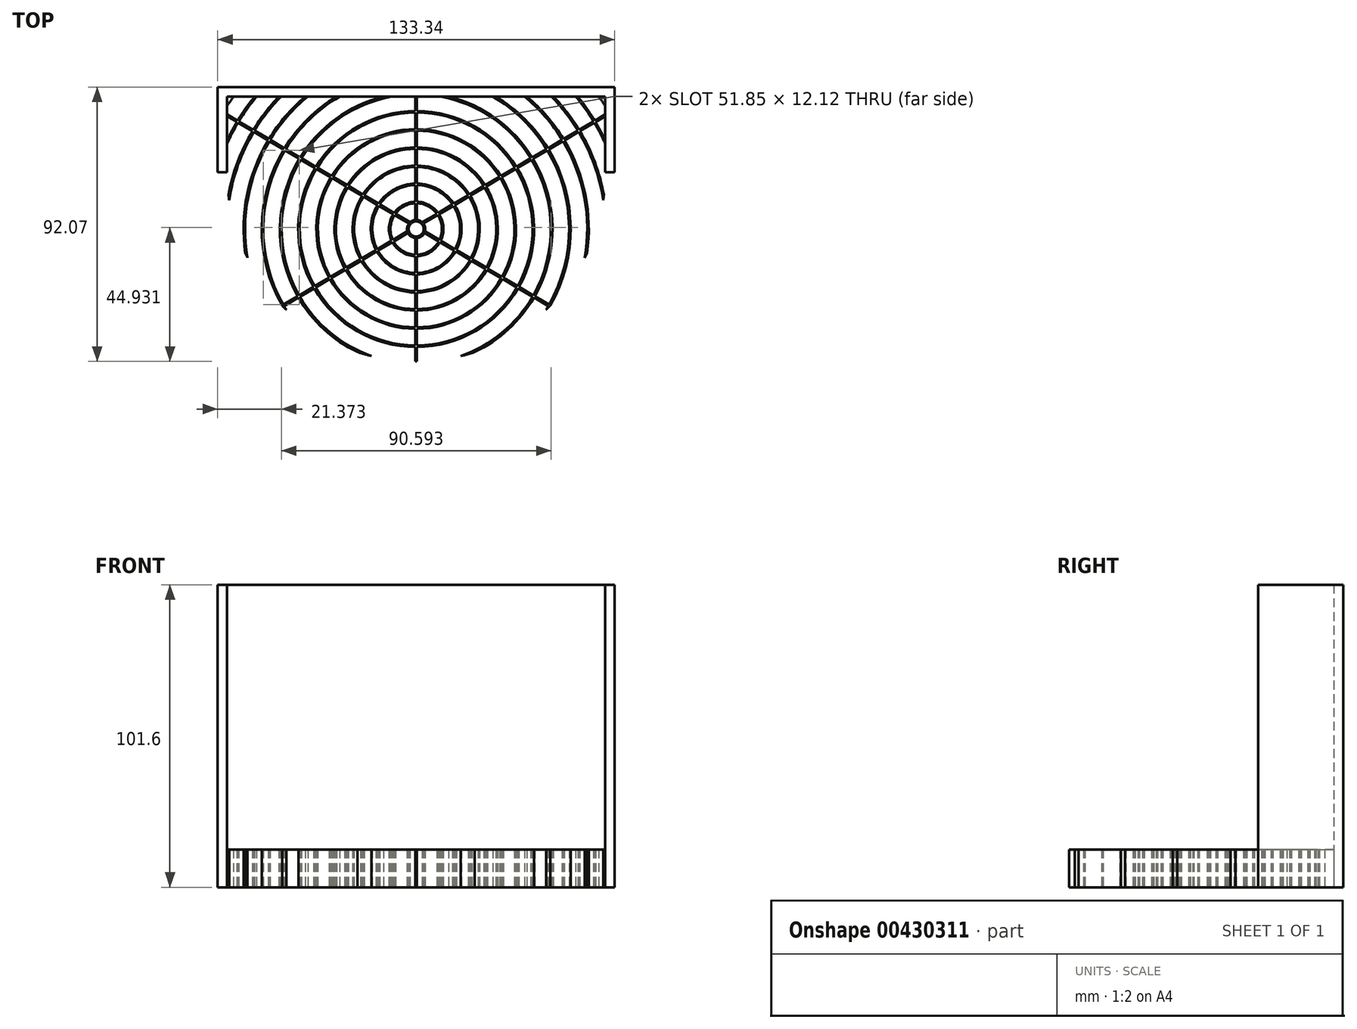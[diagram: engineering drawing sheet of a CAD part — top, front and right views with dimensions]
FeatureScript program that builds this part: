
annotation { "Feature Type Name" : "Feature", "Feature Type Description" : "" }
export const myFeature = defineFeature(function(context is Context, id is Id, definition is map)
    precondition{}
    {
        {
            var Q0;
            Q0=qCreatedBy(makeId("Top.planeOp"),FACE);
            var sketch = newSketch(context, id + "F0", { "sketchPlane" : qUnion([Q0])});
            skArc(sketch, "E0", {"start": v(63.5, 0) * mm, "mid": v(0, -63.5) * mm, "end": v(-63.5, 0) * mm});
            skArc(sketch, "E1.0", {"start": v(66.67, 0) * mm, "mid": v(0, -66.67) * mm, "end": v(-66.67, 0) * mm});
            skLineSegment(sketch, "E2.bottom", {"start": v(-66.67, 0) * mm, "end": v(-63.5, 0) * mm});
            skLineSegment(sketch, "E2.top", {"start": v(-66.67, 25.4) * mm, "end": v(-63.5, 25.4) * mm});
            skLineSegment(sketch, "E2.left", {"start": v(-66.67, 0) * mm, "end": v(-66.67, 25.4) * mm});
            skLineSegment(sketch, "E2.right", {"start": v(-63.5, 0) * mm, "end": v(-63.5, 25.4) * mm});
            skLineSegment(sketch, "E3.bottom", {"start": v(63.5, 0) * mm, "end": v(66.67, 0) * mm});
            skLineSegment(sketch, "E3.top", {"start": v(63.5, 25.4) * mm, "end": v(66.67, 25.4) * mm});
            skLineSegment(sketch, "E3.left", {"start": v(63.5, 0) * mm, "end": v(63.5, 25.4) * mm});
            skLineSegment(sketch, "E3.right", {"start": v(66.67, 0) * mm, "end": v(66.67, 25.4) * mm});
            skCircle(sketch, "E4", {"center": v(0, -19.05) * mm, "radius": 2.54 * mm});
            skArc(sketch, "E5.0", {"start": v(-0.25, -16.01) * mm, "mid": v(-1.22, -16.26) * mm, "end": v(-2.06, -16.8) * mm});
            skArc(sketch, "E6.0", {"start": v(-0.25, -10.42) * mm, "mid": v(-4, -11.4) * mm, "end": v(-6.95, -13.92) * mm});
            skArc(sketch, "E7.0", {"start": v(-0.25, -9.9) * mm, "mid": v(-4.26, -10.96) * mm, "end": v(-7.39, -13.66) * mm});
            skArc(sketch, "E8.0", {"start": v(-0.25, -4.32) * mm, "mid": v(-7.03, -6.1) * mm, "end": v(-12.22, -10.82) * mm});
            skArc(sketch, "E9.0", {"start": v(-0.25, -3.81) * mm, "mid": v(-7.28, -5.66) * mm, "end": v(-12.66, -10.56) * mm});
            skArc(sketch, "E10.0", {"start": v(-0.25, 1.78) * mm, "mid": v(-10.06, -0.81) * mm, "end": v(-17.48, -7.72) * mm});
            skArc(sketch, "E11.0", {"start": v(-0.25, 2.28) * mm, "mid": v(-10.3, -0.37) * mm, "end": v(-17.91, -7.46) * mm});
            skArc(sketch, "E12.0", {"start": v(-0.25, 7.87) * mm, "mid": v(-13.08, 4.48) * mm, "end": v(-22.73, -4.62) * mm});
            skArc(sketch, "E13.0", {"start": v(-0.25, 8.38) * mm, "mid": v(-13.33, 4.92) * mm, "end": v(-23.17, -4.36) * mm});
            skArc(sketch, "E14.0", {"start": v(-0.25, 13.97) * mm, "mid": v(-16.1, 9.78) * mm, "end": v(-27.99, -1.52) * mm});
            skArc(sketch, "E15.0", {"start": v(-0.25, 14.48) * mm, "mid": v(-16.36, 10.22) * mm, "end": v(-28.42, -1.27) * mm});
            skArc(sketch, "E16.0", {"start": v(-0.25, 20.07) * mm, "mid": v(-19.13, 15.07) * mm, "end": v(-33.24, 1.57) * mm});
            skArc(sketch, "E17.0", {"start": v(-0.25, 20.57) * mm, "mid": v(-19.38, 15.51) * mm, "end": v(-33.68, 1.83) * mm});
            skLineSegment(sketch, "E18.bottom", {"start": v(-66.67, 25.4) * mm, "end": v(66.67, 25.4) * mm});
            skLineSegment(sketch, "E18.top", {"start": v(-66.67, 28.57) * mm, "end": v(66.67, 28.57) * mm});
            skLineSegment(sketch, "E18.left", {"start": v(-66.67, 25.4) * mm, "end": v(-66.67, 28.57) * mm});
            skLineSegment(sketch, "E18.right", {"start": v(66.67, 25.4) * mm, "end": v(66.67, 28.57) * mm});
            skArc(sketch, "E19.0", {"start": v(14.98, -61.7) * mm, "mid": v(28.8, -53.9) * mm, "end": v(39.07, -41.8) * mm});
            skArc(sketch, "E20.0", {"start": v(19.68, -60.37) * mm, "mid": v(31, -52.73) * mm, "end": v(39.55, -42.09) * mm});
            skArc(sketch, "E21.0", {"start": v(43.64, -46.13) * mm, "mid": v(44, -45.53) * mm, "end": v(44.36, -44.93) * mm});
            skArc(sketch, "E22.0", {"start": v(45.05, -44.75) * mm, "mid": v(51.86, -18.5) * mm, "end": v(44.49, 7.61) * mm});
            skArc(sketch, "E23.0", {"start": v(56.64, -28.72) * mm, "mid": v(56.47, -8.48) * mm, "end": v(49.3, 10.45) * mm});
            skArc(sketch, "E24.0", {"start": v(57.4, -27.18) * mm, "mid": v(56.82, -7.58) * mm, "end": v(49.74, 10.7) * mm});
            skArc(sketch, "E25.0", {"start": v(62.8, -9.36) * mm, "mid": v(59.79, 2.5) * mm, "end": v(54.56, 13.54) * mm});
            skArc(sketch, "E26.0", {"start": v(63.04, -7.65) * mm, "mid": v(59.98, 3.44) * mm, "end": v(55, 13.8) * mm});
            skArc(sketch, "E27.0", {"start": v(63.5, 9.56) * mm, "mid": v(61.76, 13.15) * mm, "end": v(59.8, 16.64) * mm});
            skArc(sketch, "E28.0", {"start": v(63.5, 10.77) * mm, "mid": v(61.95, 13.88) * mm, "end": v(60.24, 16.9) * mm});
            skArc(sketch, "E29.0", {"start": v(63.5, 22.24) * mm, "mid": v(62.43, 23.83) * mm, "end": v(61.33, 25.4) * mm});
            skArc(sketch, "E30.trimOffspring", {"start": v(-61.33, 25.4) * mm, "mid": v(-62.43, 23.83) * mm, "end": v(-63.5, 22.24) * mm});
            skArc(sketch, "E31.trimOffspring", {"start": v(-54.28, 25.4) * mm, "mid": v(-57.27, 21.47) * mm, "end": v(-59.98, 17.33) * mm});
            skArc(sketch, "E32.trimOffspring", {"start": v(-53.62, 25.4) * mm, "mid": v(-56.73, 21.35) * mm, "end": v(-59.55, 17.08) * mm});
            skArc(sketch, "E33.trimOffspring", {"start": v(-45.42, 25.4) * mm, "mid": v(-50.18, 19.94) * mm, "end": v(-54.3, 13.98) * mm});
            skArc(sketch, "E34.trimOffspring", {"start": v(-46.13, 25.4) * mm, "mid": v(-50.74, 20.06) * mm, "end": v(-54.73, 14.24) * mm});
            skArc(sketch, "E35.trimOffspring", {"start": v(-36.4, 25.4) * mm, "mid": v(-43.33, 18.68) * mm, "end": v(-49.04, 10.88) * mm});
            skArc(sketch, "E36.trimOffspring", {"start": v(-37.2, 25.4) * mm, "mid": v(-43.92, 18.77) * mm, "end": v(-49.48, 11.14) * mm});
            skArc(sketch, "E37.trimOffspring", {"start": v(-25.73, 25.4) * mm, "mid": v(-35.86, 17.72) * mm, "end": v(-43.79, 7.79) * mm});
            skArc(sketch, "E38.trimOffspring", {"start": v(-26.73, 25.4) * mm, "mid": v(-36.52, 17.78) * mm, "end": v(-44.23, 8.05) * mm});
            skArc(sketch, "E39.trimOffspring", {"start": v(-10.92, 25.4) * mm, "mid": v(-26.96, 17.94) * mm, "end": v(-38.97, 4.95) * mm});
            skArc(sketch, "E40.trimOffspring", {"start": v(-8.27, 25.4) * mm, "mid": v(-25.57, 18.23) * mm, "end": v(-38.5, 4.67) * mm});
            skLineSegment(sketch, "E41.left", {"start": v(-0.25, 25.4) * mm, "end": v(-0.25, 20.57) * mm});
            skLineSegment(sketch, "E41.right", {"start": v(0.25, 25.4) * mm, "end": v(0.25, 20.57) * mm});
            skLineSegment(sketch, "E42.trimOffspring", {"start": v(-0.25, -22.09) * mm, "end": v(-0.25, -27.68) * mm});
            skLineSegment(sketch, "E43.trimOffspring", {"start": v(0.25, -22.09) * mm, "end": v(0.25, -27.68) * mm});
            skPoint(sketch, "E41.top.end.orphan", {"position": v(0.25, -95.25) * mm});
            skPoint(sketch, "E41.top.start.orphan", {"position": v(-0.25, -95.25) * mm});
            skPoint(sketch, "E41.bottom.end.orphan", {"position": v(0.25, 57.15) * mm});
            skPoint(sketch, "E41.bottom.start.orphan", {"position": v(-0.25, 57.15) * mm});
            skLineSegment(sketch, "E44.trimOffspring", {"start": v(-0.25, -28.2) * mm, "end": v(-0.25, -33.78) * mm});
            skLineSegment(sketch, "E45.trimOffspring", {"start": v(0.25, -28.2) * mm, "end": v(0.25, -33.78) * mm});
            skLineSegment(sketch, "E46.trimOffspring", {"start": v(0.25, -34.29) * mm, "end": v(0.25, -39.88) * mm});
            skLineSegment(sketch, "E47.trimOffspring", {"start": v(-0.25, -34.29) * mm, "end": v(-0.25, -39.88) * mm});
            skLineSegment(sketch, "E48.trimOffspring", {"start": v(0.25, -58.67) * mm, "end": v(0.25, -63.5) * mm});
            skLineSegment(sketch, "E49.trimOffspring", {"start": v(-0.25, -58.67) * mm, "end": v(-0.25, -63.5) * mm});
            skLineSegment(sketch, "E50.trimOffspring", {"start": v(-0.25, -52.58) * mm, "end": v(-0.25, -58.17) * mm});
            skLineSegment(sketch, "E51.trimOffspring", {"start": v(0.25, -52.58) * mm, "end": v(0.25, -58.17) * mm});
            skLineSegment(sketch, "E52.trimOffspring", {"start": v(-0.25, -46.48) * mm, "end": v(-0.25, -52.07) * mm});
            skLineSegment(sketch, "E53.trimOffspring", {"start": v(0.25, -46.48) * mm, "end": v(0.25, -52.07) * mm});
            skLineSegment(sketch, "E54.trimOffspring", {"start": v(0.25, -40.38) * mm, "end": v(0.25, -45.97) * mm});
            skLineSegment(sketch, "E55.trimOffspring", {"start": v(-0.25, -40.38) * mm, "end": v(-0.25, -45.97) * mm});
            skLineSegment(sketch, "E56.trimOffspring", {"start": v(0.25, -10.42) * mm, "end": v(0.25, -16.01) * mm});
            skLineSegment(sketch, "E57.trimOffspring", {"start": v(-0.25, -10.42) * mm, "end": v(-0.25, -16.01) * mm});
            skLineSegment(sketch, "E58.trimOffspring", {"start": v(0.25, -4.32) * mm, "end": v(0.25, -9.9) * mm});
            skLineSegment(sketch, "E59.trimOffspring", {"start": v(-0.25, -4.32) * mm, "end": v(-0.25, -9.9) * mm});
            skLineSegment(sketch, "E60.trimOffspring", {"start": v(0.25, 1.78) * mm, "end": v(0.25, -3.81) * mm});
            skLineSegment(sketch, "E61.trimOffspring", {"start": v(-0.25, 1.78) * mm, "end": v(-0.25, -3.81) * mm});
            skLineSegment(sketch, "E62.trimOffspring", {"start": v(-0.25, 7.87) * mm, "end": v(-0.25, 2.28) * mm});
            skLineSegment(sketch, "E63.trimOffspring", {"start": v(0.25, 7.87) * mm, "end": v(0.25, 2.28) * mm});
            skLineSegment(sketch, "E64.trimOffspring", {"start": v(0.25, 13.97) * mm, "end": v(0.25, 8.38) * mm});
            skLineSegment(sketch, "E65.trimOffspring", {"start": v(-0.25, 13.97) * mm, "end": v(-0.25, 8.38) * mm});
            skLineSegment(sketch, "E66.trimOffspring", {"start": v(0.25, 20.07) * mm, "end": v(0.25, 14.48) * mm});
            skLineSegment(sketch, "E67.trimOffspring", {"start": v(-0.25, 20.07) * mm, "end": v(-0.25, 14.48) * mm});
            skArc(sketch, "E68.trimOffspring", {"start": v(0.25, -22.09) * mm, "mid": v(1.74, -21.55) * mm, "end": v(2.76, -20.34) * mm});
            skArc(sketch, "E69.trimOffspring", {"start": v(0.25, -27.68) * mm, "mid": v(4.51, -26.41) * mm, "end": v(7.58, -23.2) * mm});
            skArc(sketch, "E70.trimOffspring", {"start": v(0.25, -28.2) * mm, "mid": v(4.77, -26.85) * mm, "end": v(8.02, -23.45) * mm});
            skArc(sketch, "E71.trimOffspring", {"start": v(0.25, -33.78) * mm, "mid": v(7.54, -31.7) * mm, "end": v(12.83, -26.3) * mm});
            skArc(sketch, "E72.trimOffspring", {"start": v(0.25, -34.29) * mm, "mid": v(7.79, -32.15) * mm, "end": v(13.26, -26.55) * mm});
            skArc(sketch, "E73.trimOffspring", {"start": v(0.25, -39.88) * mm, "mid": v(10.56, -37) * mm, "end": v(18.08, -29.4) * mm});
            skArc(sketch, "E74.trimOffspring", {"start": v(0.25, -40.38) * mm, "mid": v(10.8, -37.45) * mm, "end": v(18.51, -29.66) * mm});
            skArc(sketch, "E75.trimOffspring", {"start": v(0.25, -45.97) * mm, "mid": v(13.58, -42.3) * mm, "end": v(23.32, -32.5) * mm});
            skArc(sketch, "E76.trimOffspring", {"start": v(0.25, -46.48) * mm, "mid": v(13.83, -42.74) * mm, "end": v(23.76, -32.76) * mm});
            skArc(sketch, "E77.trimOffspring", {"start": v(0.25, -52.07) * mm, "mid": v(16.6, -47.6) * mm, "end": v(28.57, -35.6) * mm});
            skArc(sketch, "E78.trimOffspring", {"start": v(0.25, -52.58) * mm, "mid": v(16.85, -48.04) * mm, "end": v(29, -35.86) * mm});
            skArc(sketch, "E79.trimOffspring", {"start": v(0.25, -58.17) * mm, "mid": v(19.62, -52.89) * mm, "end": v(33.82, -38.7) * mm});
            skArc(sketch, "E80.trimOffspring", {"start": v(0.25, -58.67) * mm, "mid": v(19.87, -53.33) * mm, "end": v(34.26, -38.96) * mm});
            skLineSegment(sketch, "E81", {"start": v(-44.61, -44.5) * mm, "end": v(-39.8, -41.65) * mm});
            skLineSegment(sketch, "E82", {"start": v(-44.36, -44.93) * mm, "end": v(-39.55, -42.09) * mm});
            skArc(sketch, "E83.trimOffspring", {"start": v(-44.36, -44.93) * mm, "mid": v(-44, -45.53) * mm, "end": v(-43.64, -46.13) * mm});
            skLineSegment(sketch, "E84.trimOffspring", {"start": v(-39.32, -41.36) * mm, "end": v(-34.51, -38.52) * mm});
            skArc(sketch, "E85.trimOffspring", {"start": v(-39.55, -42.09) * mm, "mid": v(-31, -52.73) * mm, "end": v(-19.68, -60.37) * mm});
            skArc(sketch, "E86.trimOffspring", {"start": v(-39.07, -41.8) * mm, "mid": v(-28.8, -53.9) * mm, "end": v(-14.98, -61.7) * mm});
            skLineSegment(sketch, "E87.trimOffspring", {"start": v(-39.07, -41.8) * mm, "end": v(-34.26, -38.96) * mm});
            skArc(sketch, "E88.trimOffspring", {"start": v(-34.26, -38.96) * mm, "mid": v(-19.87, -53.33) * mm, "end": v(-0.25, -58.67) * mm});
            skArc(sketch, "E89.trimOffspring", {"start": v(-33.82, -38.7) * mm, "mid": v(-19.62, -52.89) * mm, "end": v(-0.25, -58.17) * mm});
            skLineSegment(sketch, "E90.trimOffspring", {"start": v(-34.07, -38.26) * mm, "end": v(-29.26, -35.42) * mm});
            skLineSegment(sketch, "E91.trimOffspring", {"start": v(-33.82, -38.7) * mm, "end": v(-29, -35.86) * mm});
            skLineSegment(sketch, "E92.trimOffspring", {"start": v(-28.82, -35.16) * mm, "end": v(-24.01, -32.32) * mm});
            skArc(sketch, "E93.trimOffspring", {"start": v(-29, -35.86) * mm, "mid": v(-16.85, -48.04) * mm, "end": v(-0.25, -52.58) * mm});
            skArc(sketch, "E94.trimOffspring", {"start": v(-28.57, -35.6) * mm, "mid": v(-16.6, -47.6) * mm, "end": v(-0.25, -52.07) * mm});
            skLineSegment(sketch, "E95.trimOffspring", {"start": v(-28.57, -35.6) * mm, "end": v(-23.76, -32.76) * mm});
            skArc(sketch, "E96.trimOffspring", {"start": v(-23.76, -32.76) * mm, "mid": v(-13.83, -42.74) * mm, "end": v(-0.25, -46.48) * mm});
            skLineSegment(sketch, "E97.trimOffspring", {"start": v(-23.57, -32.06) * mm, "end": v(-18.76, -29.21) * mm});
            skArc(sketch, "E98.trimOffspring", {"start": v(-23.32, -32.5) * mm, "mid": v(-13.58, -42.3) * mm, "end": v(-0.25, -45.97) * mm});
            skLineSegment(sketch, "E99.trimOffspring", {"start": v(-23.32, -32.5) * mm, "end": v(-18.51, -29.66) * mm});
            skArc(sketch, "E100.trimOffspring", {"start": v(-18.51, -29.66) * mm, "mid": v(-10.8, -37.45) * mm, "end": v(-0.25, -40.38) * mm});
            skArc(sketch, "E101.trimOffspring", {"start": v(-18.08, -29.4) * mm, "mid": v(-10.56, -37) * mm, "end": v(-0.25, -39.88) * mm});
            skLineSegment(sketch, "E102.trimOffspring", {"start": v(-18.32, -28.95) * mm, "end": v(-13.5, -26.1) * mm});
            skLineSegment(sketch, "E103.trimOffspring", {"start": v(-18.08, -29.4) * mm, "end": v(-13.26, -26.55) * mm});
            skLineSegment(sketch, "E104.trimOffspring", {"start": v(-13.07, -25.85) * mm, "end": v(-8.25, -23) * mm});
            skArc(sketch, "E105.trimOffspring", {"start": v(-13.26, -26.55) * mm, "mid": v(-7.79, -32.15) * mm, "end": v(-0.25, -34.29) * mm});
            skArc(sketch, "E106.trimOffspring", {"start": v(-12.83, -26.3) * mm, "mid": v(-7.54, -31.7) * mm, "end": v(-0.25, -33.78) * mm});
            skLineSegment(sketch, "E107.trimOffspring", {"start": v(-12.83, -26.3) * mm, "end": v(-8.02, -23.45) * mm});
            skArc(sketch, "E108.trimOffspring", {"start": v(-8.02, -23.45) * mm, "mid": v(-4.77, -26.85) * mm, "end": v(-0.25, -28.2) * mm});
            skArc(sketch, "E109.trimOffspring", {"start": v(-7.58, -23.2) * mm, "mid": v(-4.51, -26.41) * mm, "end": v(-0.25, -27.68) * mm});
            skLineSegment(sketch, "E110.trimOffspring", {"start": v(-7.8, -22.74) * mm, "end": v(-2.94, -19.86) * mm});
            skLineSegment(sketch, "E111.trimOffspring", {"start": v(-7.58, -23.2) * mm, "end": v(-2.76, -20.34) * mm});
            skArc(sketch, "E112.trimOffspring", {"start": v(-2.76, -20.34) * mm, "mid": v(-1.74, -21.55) * mm, "end": v(-0.25, -22.09) * mm});
            skLineSegment(sketch, "E113", {"start": v(2.41, -17.19) * mm, "end": v(7.24, -14.34) * mm});
            skLineSegment(sketch, "E114", {"start": v(2.06, -16.8) * mm, "end": v(6.95, -13.92) * mm});
            skArc(sketch, "E115.trimOffspring", {"start": v(2.06, -16.8) * mm, "mid": v(1.22, -16.26) * mm, "end": v(0.25, -16.01) * mm});
            skArc(sketch, "E116.trimOffspring", {"start": v(6.95, -13.92) * mm, "mid": v(4, -11.4) * mm, "end": v(0.25, -10.42) * mm});
            skLineSegment(sketch, "E117.trimOffspring", {"start": v(7.39, -13.66) * mm, "end": v(12.22, -10.82) * mm});
            skArc(sketch, "E118.trimOffspring", {"start": v(7.39, -13.66) * mm, "mid": v(4.26, -10.96) * mm, "end": v(0.25, -9.9) * mm});
            skLineSegment(sketch, "E119.trimOffspring", {"start": v(7.68, -14.08) * mm, "end": v(12.5, -11.24) * mm});
            skArc(sketch, "E120.trimOffspring", {"start": v(12.22, -10.82) * mm, "mid": v(7.03, -6.1) * mm, "end": v(0.25, -4.32) * mm});
            skLineSegment(sketch, "E121.trimOffspring", {"start": v(12.66, -10.56) * mm, "end": v(17.48, -7.72) * mm});
            skArc(sketch, "E122.trimOffspring", {"start": v(12.66, -10.56) * mm, "mid": v(7.28, -5.66) * mm, "end": v(0.25, -3.81) * mm});
            skLineSegment(sketch, "E123.trimOffspring", {"start": v(12.93, -10.99) * mm, "end": v(17.75, -8.15) * mm});
            skArc(sketch, "E124.trimOffspring", {"start": v(17.48, -7.72) * mm, "mid": v(10.06, -0.81) * mm, "end": v(0.25, 1.78) * mm});
            skLineSegment(sketch, "E125.trimOffspring", {"start": v(17.91, -7.46) * mm, "end": v(22.73, -4.62) * mm});
            skArc(sketch, "E126.trimOffspring", {"start": v(17.91, -7.46) * mm, "mid": v(10.3, -0.37) * mm, "end": v(0.25, 2.28) * mm});
            skLineSegment(sketch, "E127.trimOffspring", {"start": v(18.18, -7.89) * mm, "end": v(23, -5.05) * mm});
            skArc(sketch, "E128.trimOffspring", {"start": v(22.73, -4.62) * mm, "mid": v(13.08, 4.48) * mm, "end": v(0.25, 7.87) * mm});
            skArc(sketch, "E129.trimOffspring", {"start": v(23.17, -4.36) * mm, "mid": v(13.33, 4.92) * mm, "end": v(0.25, 8.38) * mm});
            skLineSegment(sketch, "E130.trimOffspring", {"start": v(23.17, -4.36) * mm, "end": v(27.99, -1.52) * mm});
            skLineSegment(sketch, "E131.trimOffspring", {"start": v(23.44, -4.8) * mm, "end": v(28.25, -1.96) * mm});
            skArc(sketch, "E132.trimOffspring", {"start": v(27.99, -1.52) * mm, "mid": v(16.1, 9.78) * mm, "end": v(0.25, 13.97) * mm});
            skLineSegment(sketch, "E133.trimOffspring", {"start": v(28.42, -1.27) * mm, "end": v(33.24, 1.57) * mm});
            skArc(sketch, "E134.trimOffspring", {"start": v(28.42, -1.27) * mm, "mid": v(16.36, 10.22) * mm, "end": v(0.25, 14.48) * mm});
            skLineSegment(sketch, "E135.trimOffspring", {"start": v(28.69, -1.7) * mm, "end": v(33.5, 1.14) * mm});
            skArc(sketch, "E136.trimOffspring", {"start": v(33.24, 1.57) * mm, "mid": v(19.13, 15.07) * mm, "end": v(0.25, 20.07) * mm});
            skArc(sketch, "E137.trimOffspring", {"start": v(33.68, 1.83) * mm, "mid": v(19.38, 15.51) * mm, "end": v(0.25, 20.57) * mm});
            skLineSegment(sketch, "E138.trimOffspring", {"start": v(33.68, 1.83) * mm, "end": v(38.5, 4.67) * mm});
            skLineSegment(sketch, "E139.trimOffspring", {"start": v(33.94, 1.4) * mm, "end": v(38.76, 4.23) * mm});
            skLineSegment(sketch, "E140.trimOffspring", {"start": v(38.97, 4.95) * mm, "end": v(43.79, 7.79) * mm});
            skArc(sketch, "E141.trimOffspring", {"start": v(38.5, 4.67) * mm, "mid": v(25.57, 18.23) * mm, "end": v(8.27, 25.4) * mm});
            skArc(sketch, "E142.trimOffspring", {"start": v(38.97, 4.95) * mm, "mid": v(26.96, 17.94) * mm, "end": v(10.92, 25.4) * mm});
            skLineSegment(sketch, "E143.trimOffspring", {"start": v(39.24, 4.52) * mm, "end": v(44.05, 7.35) * mm});
            skArc(sketch, "E144.trimOffspring", {"start": v(43.79, 7.79) * mm, "mid": v(35.86, 17.72) * mm, "end": v(25.73, 25.4) * mm});
            skLineSegment(sketch, "E145.trimOffspring", {"start": v(44.23, 8.05) * mm, "end": v(49.04, 10.88) * mm});
            skArc(sketch, "E146.trimOffspring", {"start": v(44.23, 8.05) * mm, "mid": v(36.52, 17.78) * mm, "end": v(26.73, 25.4) * mm});
            skLineSegment(sketch, "E147.trimOffspring", {"start": v(44.49, 7.61) * mm, "end": v(49.3, 10.45) * mm});
            skArc(sketch, "E148.trimOffspring", {"start": v(49.04, 10.88) * mm, "mid": v(43.33, 18.68) * mm, "end": v(36.4, 25.4) * mm});
            skLineSegment(sketch, "E149.trimOffspring", {"start": v(49.48, 11.14) * mm, "end": v(54.3, 13.98) * mm});
            skArc(sketch, "E150.trimOffspring", {"start": v(49.48, 11.14) * mm, "mid": v(43.92, 18.77) * mm, "end": v(37.2, 25.4) * mm});
            skLineSegment(sketch, "E151.trimOffspring", {"start": v(49.74, 10.7) * mm, "end": v(54.56, 13.54) * mm});
            skArc(sketch, "E152.trimOffspring", {"start": v(54.3, 13.98) * mm, "mid": v(50.18, 19.94) * mm, "end": v(45.42, 25.4) * mm});
            skLineSegment(sketch, "E153.trimOffspring", {"start": v(54.73, 14.24) * mm, "end": v(59.55, 17.08) * mm});
            skArc(sketch, "E154.trimOffspring", {"start": v(54.73, 14.24) * mm, "mid": v(50.74, 20.06) * mm, "end": v(46.13, 25.4) * mm});
            skLineSegment(sketch, "E155.trimOffspring", {"start": v(55, 13.8) * mm, "end": v(59.8, 16.64) * mm});
            skArc(sketch, "E156.trimOffspring", {"start": v(59.55, 17.08) * mm, "mid": v(56.73, 21.35) * mm, "end": v(53.62, 25.4) * mm});
            skArc(sketch, "E157.trimOffspring", {"start": v(59.98, 17.33) * mm, "mid": v(57.27, 21.47) * mm, "end": v(54.28, 25.4) * mm});
            skLineSegment(sketch, "E158.trimOffspring", {"start": v(59.98, 17.33) * mm, "end": v(63.5, 19.4) * mm});
            skLineSegment(sketch, "E159.trimOffspring", {"start": v(60.24, 16.9) * mm, "end": v(63.5, 18.82) * mm});
            skLineSegment(sketch, "E160", {"start": v(2.94, -19.86) * mm, "end": v(7.8, -22.74) * mm});
            skLineSegment(sketch, "E161", {"start": v(2.76, -20.34) * mm, "end": v(7.58, -23.2) * mm});
            skLineSegment(sketch, "E162", {"start": v(-2.06, -16.8) * mm, "end": v(-6.95, -13.92) * mm});
            skLineSegment(sketch, "E163", {"start": v(-2.41, -17.19) * mm, "end": v(-7.24, -14.34) * mm});
            skArc(sketch, "E164.trimOffspring", {"start": v(-2.41, -17.19) * mm, "mid": v(-3, -18.46) * mm, "end": v(-2.94, -19.86) * mm});
            skLineSegment(sketch, "E165.trimOffspring", {"start": v(-7.39, -13.66) * mm, "end": v(-12.22, -10.82) * mm});
            skArc(sketch, "E166.trimOffspring", {"start": v(-7.68, -14.08) * mm, "mid": v(-9.13, -18.47) * mm, "end": v(-8.25, -23) * mm});
            skLineSegment(sketch, "E167.trimOffspring", {"start": v(-7.68, -14.08) * mm, "end": v(-12.5, -11.24) * mm});
            skArc(sketch, "E168.trimOffspring", {"start": v(-7.24, -14.34) * mm, "mid": v(-8.62, -18.47) * mm, "end": v(-7.8, -22.74) * mm});
            skArc(sketch, "E169.trimOffspring", {"start": v(-12.5, -11.24) * mm, "mid": v(-14.72, -18.47) * mm, "end": v(-13.07, -25.85) * mm});
            skArc(sketch, "E170.trimOffspring", {"start": v(-12.93, -10.99) * mm, "mid": v(-15.23, -18.47) * mm, "end": v(-13.5, -26.1) * mm});
            skLineSegment(sketch, "E171.trimOffspring", {"start": v(-12.66, -10.56) * mm, "end": v(-17.48, -7.72) * mm});
            skLineSegment(sketch, "E172.trimOffspring", {"start": v(-12.93, -10.99) * mm, "end": v(-17.75, -8.15) * mm});
            skArc(sketch, "E173.trimOffspring", {"start": v(-18.18, -7.89) * mm, "mid": v(-21.33, -18.47) * mm, "end": v(-18.76, -29.21) * mm});
            skLineSegment(sketch, "E174.trimOffspring", {"start": v(-17.91, -7.46) * mm, "end": v(-22.73, -4.62) * mm});
            skLineSegment(sketch, "E175.trimOffspring", {"start": v(-18.18, -7.89) * mm, "end": v(-23, -5.05) * mm});
            skArc(sketch, "E176.trimOffspring", {"start": v(-17.75, -8.15) * mm, "mid": v(-20.82, -18.47) * mm, "end": v(-18.32, -28.95) * mm});
            skArc(sketch, "E177.trimOffspring", {"start": v(-23.44, -4.8) * mm, "mid": v(-27.43, -18.48) * mm, "end": v(-24.01, -32.32) * mm});
            skLineSegment(sketch, "E178.trimOffspring", {"start": v(-23.17, -4.36) * mm, "end": v(-27.99, -1.52) * mm});
            skLineSegment(sketch, "E179.trimOffspring", {"start": v(-23.44, -4.8) * mm, "end": v(-28.25, -1.96) * mm});
            skArc(sketch, "E180.trimOffspring", {"start": v(-23, -5.05) * mm, "mid": v(-26.92, -18.48) * mm, "end": v(-23.57, -32.06) * mm});
            skLineSegment(sketch, "E181.trimOffspring", {"start": v(-28.42, -1.27) * mm, "end": v(-33.24, 1.57) * mm});
            skArc(sketch, "E182.trimOffspring", {"start": v(-28.69, -1.7) * mm, "mid": v(-33.52, -18.48) * mm, "end": v(-29.26, -35.42) * mm});
            skArc(sketch, "E183.trimOffspring", {"start": v(-28.25, -1.96) * mm, "mid": v(-33.02, -18.48) * mm, "end": v(-28.82, -35.16) * mm});
            skLineSegment(sketch, "E184.trimOffspring", {"start": v(-28.69, -1.7) * mm, "end": v(-33.5, 1.14) * mm});
            skLineSegment(sketch, "E185.trimOffspring", {"start": v(-33.68, 1.83) * mm, "end": v(-38.5, 4.67) * mm});
            skArc(sketch, "E186.trimOffspring", {"start": v(-33.94, 1.4) * mm, "mid": v(-39.62, -18.49) * mm, "end": v(-34.51, -38.52) * mm});
            skArc(sketch, "E187.trimOffspring", {"start": v(-33.5, 1.14) * mm, "mid": v(-39.11, -18.48) * mm, "end": v(-34.07, -38.26) * mm});
            skLineSegment(sketch, "E188.trimOffspring", {"start": v(-33.94, 1.4) * mm, "end": v(-38.76, 4.23) * mm});
            skLineSegment(sketch, "E189.trimOffspring", {"start": v(-38.97, 4.95) * mm, "end": v(-43.79, 7.79) * mm});
            skArc(sketch, "E190.trimOffspring", {"start": v(-39.24, 4.52) * mm, "mid": v(-45.77, -18.49) * mm, "end": v(-39.8, -41.65) * mm});
            skArc(sketch, "E191.trimOffspring", {"start": v(-38.76, 4.23) * mm, "mid": v(-45.2, -18.49) * mm, "end": v(-39.32, -41.36) * mm});
            skLineSegment(sketch, "E192.trimOffspring", {"start": v(-39.24, 4.52) * mm, "end": v(-44.05, 7.35) * mm});
            skArc(sketch, "E193.trimOffspring", {"start": v(-44.49, 7.61) * mm, "mid": v(-51.86, -18.5) * mm, "end": v(-45.05, -44.75) * mm});
            skArc(sketch, "E194.trimOffspring", {"start": v(-44.05, 7.35) * mm, "mid": v(-51.36, -18.5) * mm, "end": v(-44.61, -44.5) * mm});
            skLineSegment(sketch, "E195.trimOffspring", {"start": v(-44.23, 8.05) * mm, "end": v(-49.04, 10.88) * mm});
            skLineSegment(sketch, "E196.trimOffspring", {"start": v(-44.49, 7.61) * mm, "end": v(-49.3, 10.45) * mm});
            skArc(sketch, "E197.trimOffspring", {"start": v(-49.74, 10.7) * mm, "mid": v(-56.82, -7.58) * mm, "end": v(-57.4, -27.18) * mm});
            skLineSegment(sketch, "E198.trimOffspring", {"start": v(-49.48, 11.14) * mm, "end": v(-54.3, 13.98) * mm});
            skArc(sketch, "E199.trimOffspring", {"start": v(-49.3, 10.45) * mm, "mid": v(-56.47, -8.48) * mm, "end": v(-56.64, -28.72) * mm});
            skLineSegment(sketch, "E200.trimOffspring", {"start": v(-49.74, 10.7) * mm, "end": v(-54.56, 13.54) * mm});
            skLineSegment(sketch, "E201.trimOffspring", {"start": v(-54.73, 14.24) * mm, "end": v(-59.55, 17.08) * mm});
            skArc(sketch, "E202.trimOffspring", {"start": v(-55, 13.8) * mm, "mid": v(-59.98, 3.44) * mm, "end": v(-63.04, -7.65) * mm});
            skArc(sketch, "E203.trimOffspring", {"start": v(-54.56, 13.54) * mm, "mid": v(-59.79, 2.5) * mm, "end": v(-62.8, -9.36) * mm});
            skLineSegment(sketch, "E204.trimOffspring", {"start": v(-55, 13.8) * mm, "end": v(-59.8, 16.64) * mm});
            skLineSegment(sketch, "E205.trimOffspring", {"start": v(-59.98, 17.33) * mm, "end": v(-63.5, 19.4) * mm});
            skArc(sketch, "E206.trimOffspring", {"start": v(-59.8, 16.64) * mm, "mid": v(-61.76, 13.15) * mm, "end": v(-63.5, 9.56) * mm});
            skLineSegment(sketch, "E207.trimOffspring", {"start": v(-60.24, 16.9) * mm, "end": v(-63.5, 18.82) * mm});
            skArc(sketch, "E208.trimOffspring", {"start": v(-60.24, 16.9) * mm, "mid": v(-61.95, 13.88) * mm, "end": v(-63.5, 10.77) * mm});
            skArc(sketch, "E209.trimOffspring", {"start": v(44.61, -44.5) * mm, "mid": v(51.36, -18.5) * mm, "end": v(44.05, 7.35) * mm});
            skArc(sketch, "E210.trimOffspring", {"start": v(39.8, -41.65) * mm, "mid": v(45.77, -18.49) * mm, "end": v(39.24, 4.52) * mm});
            skArc(sketch, "E211.trimOffspring", {"start": v(39.32, -41.36) * mm, "mid": v(45.2, -18.49) * mm, "end": v(38.76, 4.23) * mm});
            skLineSegment(sketch, "E212.trimOffspring", {"start": v(39.8, -41.65) * mm, "end": v(44.61, -44.5) * mm});
            skLineSegment(sketch, "E213.trimOffspring", {"start": v(39.55, -42.09) * mm, "end": v(44.36, -44.93) * mm});
            skArc(sketch, "E214.trimOffspring", {"start": v(34.07, -38.26) * mm, "mid": v(39.11, -18.48) * mm, "end": v(33.5, 1.14) * mm});
            skLineSegment(sketch, "E215.trimOffspring", {"start": v(34.51, -38.52) * mm, "end": v(39.32, -41.36) * mm});
            skArc(sketch, "E216.trimOffspring", {"start": v(34.51, -38.52) * mm, "mid": v(39.62, -18.49) * mm, "end": v(33.94, 1.4) * mm});
            skLineSegment(sketch, "E217.trimOffspring", {"start": v(34.26, -38.96) * mm, "end": v(39.07, -41.8) * mm});
            skArc(sketch, "E218.trimOffspring", {"start": v(28.82, -35.16) * mm, "mid": v(33.02, -18.48) * mm, "end": v(28.25, -1.96) * mm});
            skLineSegment(sketch, "E219.trimOffspring", {"start": v(29.26, -35.42) * mm, "end": v(34.07, -38.26) * mm});
            skArc(sketch, "E220.trimOffspring", {"start": v(29.26, -35.42) * mm, "mid": v(33.52, -18.48) * mm, "end": v(28.69, -1.7) * mm});
            skLineSegment(sketch, "E221.trimOffspring", {"start": v(29, -35.86) * mm, "end": v(33.82, -38.7) * mm});
            skArc(sketch, "E222.trimOffspring", {"start": v(24.01, -32.32) * mm, "mid": v(27.43, -18.48) * mm, "end": v(23.44, -4.8) * mm});
            skLineSegment(sketch, "E223.trimOffspring", {"start": v(24.01, -32.32) * mm, "end": v(28.82, -35.16) * mm});
            skArc(sketch, "E224.trimOffspring", {"start": v(23.57, -32.06) * mm, "mid": v(26.92, -18.48) * mm, "end": v(23, -5.05) * mm});
            skLineSegment(sketch, "E225.trimOffspring", {"start": v(23.76, -32.76) * mm, "end": v(28.57, -35.6) * mm});
            skArc(sketch, "E226.trimOffspring", {"start": v(18.32, -28.95) * mm, "mid": v(20.82, -18.47) * mm, "end": v(17.75, -8.15) * mm});
            skLineSegment(sketch, "E227.trimOffspring", {"start": v(18.76, -29.21) * mm, "end": v(23.57, -32.06) * mm});
            skArc(sketch, "E228.trimOffspring", {"start": v(18.76, -29.21) * mm, "mid": v(21.33, -18.47) * mm, "end": v(18.18, -7.89) * mm});
            skLineSegment(sketch, "E229.trimOffspring", {"start": v(18.51, -29.66) * mm, "end": v(23.32, -32.5) * mm});
            skArc(sketch, "E230.trimOffspring", {"start": v(2.94, -19.86) * mm, "mid": v(3, -18.46) * mm, "end": v(2.41, -17.19) * mm});
            skLineSegment(sketch, "E231.trimOffspring", {"start": v(8.25, -23) * mm, "end": v(13.07, -25.85) * mm});
            skArc(sketch, "E232.trimOffspring", {"start": v(7.8, -22.74) * mm, "mid": v(8.62, -18.47) * mm, "end": v(7.24, -14.34) * mm});
            skLineSegment(sketch, "E233.trimOffspring", {"start": v(8.02, -23.45) * mm, "end": v(12.83, -26.3) * mm});
            skArc(sketch, "E234.trimOffspring", {"start": v(8.25, -23) * mm, "mid": v(9.13, -18.47) * mm, "end": v(7.68, -14.08) * mm});
            skLineSegment(sketch, "E235.trimOffspring", {"start": v(13.5, -26.1) * mm, "end": v(18.32, -28.95) * mm});
            skArc(sketch, "E236.trimOffspring", {"start": v(13.07, -25.85) * mm, "mid": v(14.72, -18.47) * mm, "end": v(12.5, -11.24) * mm});
            skLineSegment(sketch, "E237.trimOffspring", {"start": v(13.26, -26.55) * mm, "end": v(18.08, -29.4) * mm});
            skArc(sketch, "E238.trimOffspring", {"start": v(13.5, -26.1) * mm, "mid": v(15.23, -18.47) * mm, "end": v(12.93, -10.99) * mm});
            skSolve(sketch);
        }
        {
            var Q0;
            Q0=makeQuery(id+"F0.imprint","IMPRINT",FACE,{"disambiguationData":[TD([[makeQuery(id+"F0.imprint","IMPRINT",EDGE,{"derivedFrom":sQuery(id+"F0.wireOp",EDGE,"E4")}),-1.0]])]});
            var Q1;
            {var subQ3=sQuery(id+"F0.wireOp",EDGE,"E29.0");Q1=makeQuery(id+"F0.imprint","IMPRINT",FACE,{"disambiguationData":[TD([[makeQuery(id+"F0.imprint","IMPRINT",EDGE,{"derivedFrom":subQ3}),-1.0]])]});}
            var Q2;
            {var subQ3=sQuery(id+"F0.wireOp",EDGE,"E30.trimOffspring");Q2=makeQuery(id+"F0.imprint","IMPRINT",FACE,{"disambiguationData":[TD([[makeQuery(id+"F0.imprint","IMPRINT",EDGE,{"derivedFrom":subQ3}),-1.0]])]});}
            extrude(context, id + "F1", {"entities" : qUnion([Q0, Q1, Q2]), "depth" : 12.7 * mm});
        }
        {
            var Q0;
            Q0=makeQuery(id+"F0.imprint","IMPRINT",FACE,{"disambiguationData":[TD([[makeQuery(id+"F0.imprint","IMPRINT",EDGE,{"derivedFrom":sQuery(id+"F0.wireOp",EDGE,"E18.top")}),-1.0]])]});
            var Q1;
            {var subQ3=sQuery(id+"F0.wireOp",EDGE,"E2.bottom");Q1=makeQuery(id+"F0.imprint","IMPRINT",FACE,{"disambiguationData":[TD([[makeQuery(id+"F0.imprint","IMPRINT",EDGE,{"derivedFrom":subQ3}),1.0]])]});}
            var Q2;
            {var subQ4=sQuery(id+"F0.wireOp",EDGE,"E3.bottom");Q2=makeQuery(id+"F0.imprint","IMPRINT",FACE,{"disambiguationData":[TD([[makeQuery(id+"F0.imprint","IMPRINT",EDGE,{"derivedFrom":subQ4}),1.0]])]});}
            var Q3;
            Q3=makeQuery(id+"F0.imprint","IMPRINT",FACE,{"disambiguationData":[TD([[makeQuery(id+"F0.imprint","IMPRINT",EDGE,{"derivedFrom":sQuery(id+"F0.wireOp",EDGE,"E1.0")}),-1.0]])]});
            extrude(context, id + "F2", {"entities" : qUnion([Q0, Q1, Q2, Q3]), "depth" : 101.6 * mm});
        }
    });
